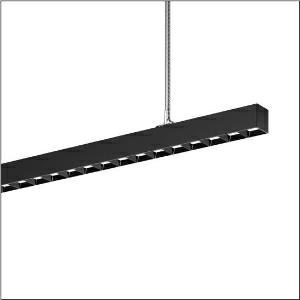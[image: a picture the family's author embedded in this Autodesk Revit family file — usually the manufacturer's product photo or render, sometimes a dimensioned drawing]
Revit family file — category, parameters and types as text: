
# Revit family: silica_r__21_51mx31dc4dbb_76cd
name_source: partatom
category: Lighting Fixtures
units: mm (PartAtom-declared; Revit-internal decimal feet)

## family parameters
Cut with Voids When Loaded = No
Host = Face
Light Source = No
Part Type = Normal
Room Calculation Point = No
Round Connector Dimension = Use Diameter
Shared = No

## types (1)
- --- (1 x LED, 18230 lm, 105.9 W, 4000K)
    Apparent Load = 106 VA
    CIE Flux Codes = 87 99 100 59 100
    Color Rendering = 80
    Color Temperature = 4000K
    Default Elevation = 1800 mm
    Description = Silica® 21, office luminaire, primary light control with darklight reflector, of PMMA, black, CAT 2 (L<= 3000cd/m²), light emission: direct/indirect distribution, primary light characteristic: symmetric, installation type: suspended mounting, LED, rated luminous flux: 18.230lm, luminous efficacy: 172lm/W, light colour: 840, colour temperature: 4000K, with terminal, 3+2-pole, max. 2.5mm², mains connection: 220..240V, AC, 50/60Hz, rated input power: 105.9W, luminaire housing, of aluminium, jet black (RAL 9005), length: 3.004mm, width: 53mm, height: 53mm, protection rating (complete): IP20, insulation class (complete): insulation class I (protective earthing), certification: CE, permissible operating ambient temperature: 0..+35°C, standard: EN 50419, packaging unit: 1 piece
    Height = 53 mm
    Lamp = 1 x LED
    Lamp Light Flux = 18230 lm
    Lamp Power = 105.9 W
    Lamp count = 1
    Length = 3004 mm
    Luminous efficacy = 172 lm/W
    Manufacturer = Siteco
    ModVariant = No
    Model = 51MX31DC4DBB
    Mounting Place = Ceiling
    Mounting Type = Pendant
    Number of Poles = 1
    OnlyDefault = Yes
    Power Factor = 1
    Product Name = Silica® 21
    Product group = office luminaire | ceiling pendant
    ProductGroupID = 902
    Protection Class = Protection class I
    Protection Degree = IP 20
    RLX_Detail_Level = 1
    RLX_Emergency_Light_Flux = 0 lm
    RLX_Emergency_Type = 0
    RLX_Emergency_Type_DB = No
    RlxData = <blob elided: 67185 chars, md5=1acdbd59>
    Socket = socket
    Standby Power = 0 W
    System Light Flux = 18230 lm
    System Power = 106 W
    Type Comments = factory setting: luminous flux: 100 % | dim-lin: 254 | 367 mA
    Type Image = l_1335852.jpg
    URL = http://relux.com
    VarID = @adj_090605
    Voltage = 0 V
    Weight = 0.00 kg
    Width = 53 mm

## geometry (parser evidence)
native form markers: Blend x4, Sweep x13
no freeform markers — native parametric forms only
